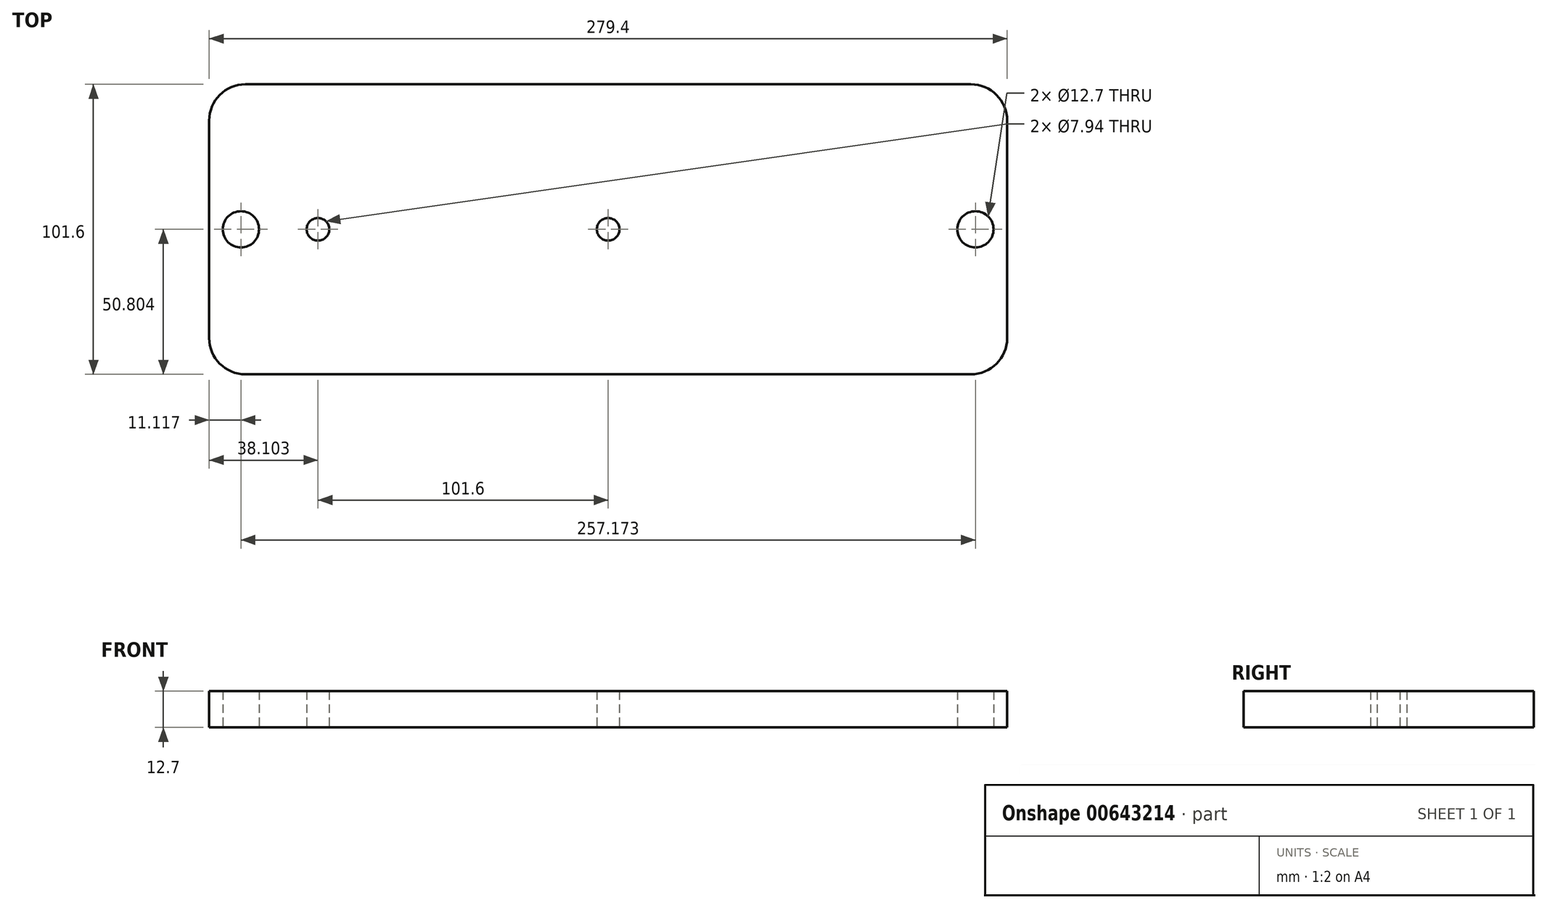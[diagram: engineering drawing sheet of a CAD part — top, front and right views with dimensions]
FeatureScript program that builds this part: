
annotation { "Feature Type Name" : "Feature", "Feature Type Description" : "" }
export const myFeature = defineFeature(function(context is Context, id is Id, definition is map)
    precondition{}
    {
        {
            var Q0;
            Q0=qCreatedBy(makeId("Top.planeOp"),FACE);
            var sketch = newSketch(context, id + "F0", { "sketchPlane" : qUnion([Q0])});
            skLineSegment(sketch, "E0", {"start": v(-67.23, 59.64) * mm, "end": v(186.77, 59.64) * mm});
            skLineSegment(sketch, "E1", {"start": v(199.47, 46.94) * mm, "end": v(199.47, -29.26) * mm});
            skLineSegment(sketch, "E2", {"start": v(186.77, -41.96) * mm, "end": v(-67.23, -41.96) * mm});
            skLineSegment(sketch, "E3", {"start": v(-79.93, -29.26) * mm, "end": v(-79.93, 46.94) * mm});
            skPoint(sketch, "E4.visualSharp", {"position": v(-79.93, 59.64) * mm});
            skArc(sketch, "E4.filletArc", {"start": v(-67.23, 59.64) * mm, "mid": v(-76.2, 55.92) * mm, "end": v(-79.93, 46.94) * mm});
            skPoint(sketch, "E5.visualSharp", {"position": v(199.47, 59.64) * mm});
            skArc(sketch, "E5.filletArc", {"start": v(199.47, 46.94) * mm, "mid": v(195.75, 55.92) * mm, "end": v(186.77, 59.64) * mm});
            skPoint(sketch, "E6.visualSharp", {"position": v(199.47, -41.96) * mm});
            skArc(sketch, "E6.filletArc", {"start": v(186.77, -41.96) * mm, "mid": v(195.75, -38.24) * mm, "end": v(199.47, -29.26) * mm});
            skPoint(sketch, "E7.visualSharp", {"position": v(-79.93, -41.96) * mm});
            skArc(sketch, "E7.filletArc", {"start": v(-79.93, -29.26) * mm, "mid": v(-76.2, -38.24) * mm, "end": v(-67.23, -41.96) * mm});
            skLineSegment(sketch, "E8", {"start": v(-85.16, 8.84) * mm, "end": v(204.7, 8.84) * mm, "construction": true});
            skPoint(sketch, "E8.startSnap0", {"position": v(-79.93, 8.84) * mm});
            skCircle(sketch, "E9", {"center": v(-68.81, 8.84) * mm, "radius": 6.35 * mm});
            skCircle(sketch, "E10", {"center": v(-41.83, 8.84) * mm, "radius": 3.97 * mm});
            skCircle(sketch, "E11", {"center": v(59.77, 8.84) * mm, "radius": 3.97 * mm});
            skCircle(sketch, "E12", {"center": v(188.36, 8.84) * mm, "radius": 6.35 * mm});
            skSolve(sketch);
        }
        {
            var Q0;
            Q0 = qSketchRegion(id + "F0", true);
            extrude(context, id + "F1", {"entities" : qUnion([Q0]), "endBound" : BoundingType.SYMMETRIC, "depth" : 12.7 * mm, "offsetDistance" : 25.4 * mm});
        }
    });
